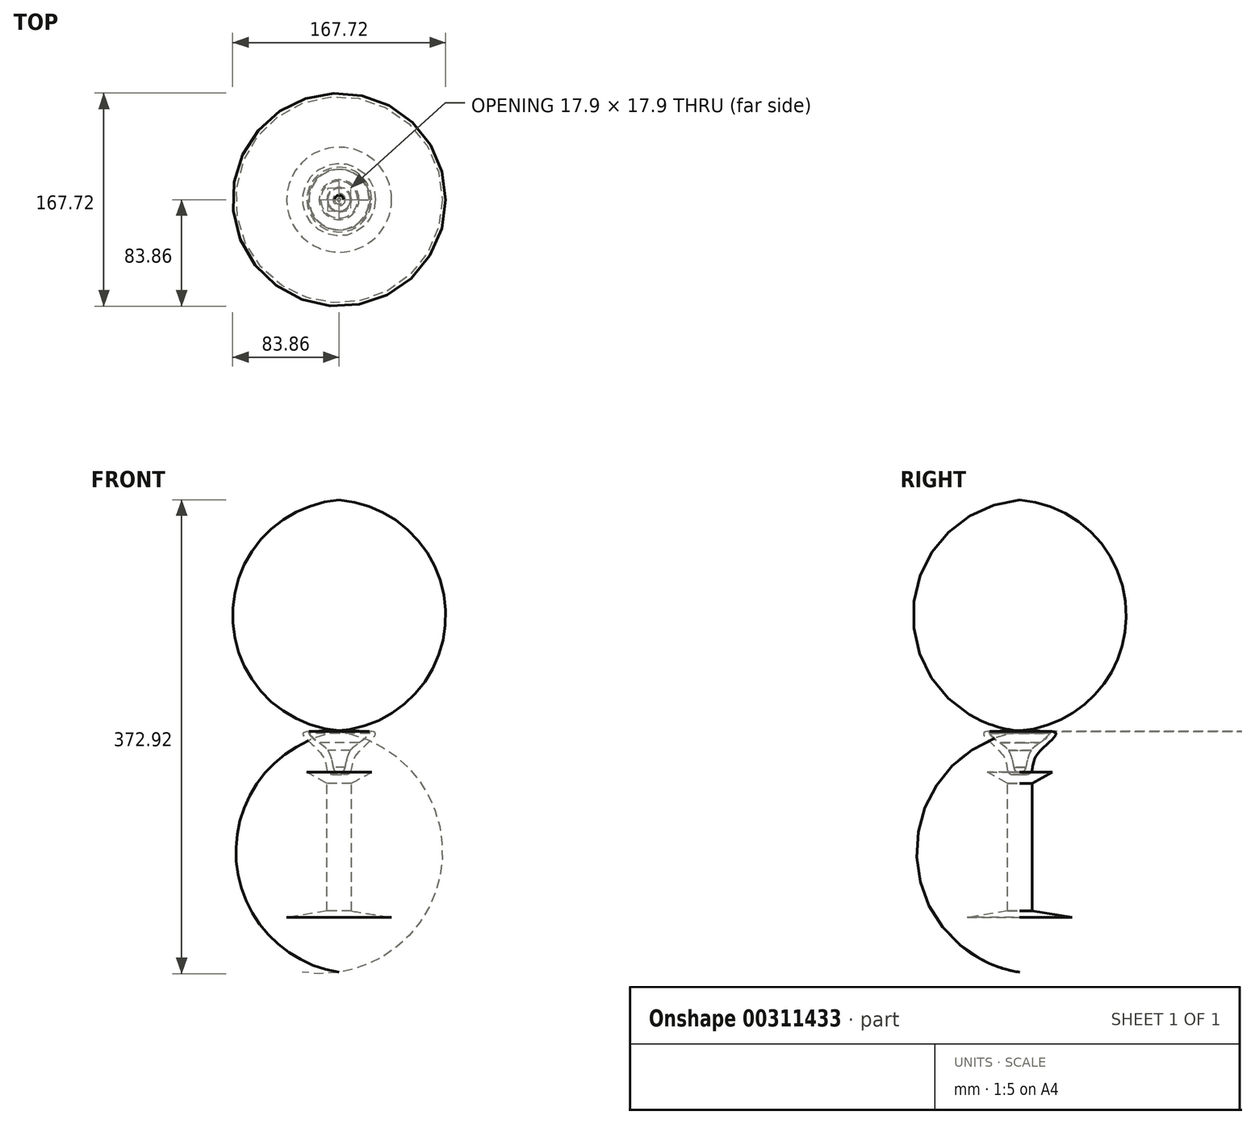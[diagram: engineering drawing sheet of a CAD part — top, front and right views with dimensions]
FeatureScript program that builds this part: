
annotation { "Feature Type Name" : "Feature", "Feature Type Description" : "" }
export const myFeature = defineFeature(function(context is Context, id is Id, definition is map)
    precondition{}
    {
        {
            var Q0;
            Q0=qCreatedBy(makeId("Front.planeOp"),FACE);
            var sketch = newSketch(context, id + "F0", { "sketchPlane" : qUnion([Q0])});
            skLineSegment(sketch, "E0", {"start": v(0, 76.77) * mm, "end": v(0, -76.43) * mm, "construction": true});
            skLineSegment(sketch, "E1", {"start": v(0, -76.43) * mm, "end": v(-41.31, -76.43) * mm});
            skLineSegment(sketch, "E2", {"start": v(-9.64, -71.26) * mm, "end": v(-9.64, 29.26) * mm});
            skLineSegment(sketch, "E3", {"start": v(-25.48, 37.87) * mm, "end": v(-8.95, 37.87) * mm});
            skLineSegment(sketch, "E4", {"start": v(0, 37.87) * mm, "end": v(0, -76.43) * mm});
            skFitSpline(sketch, "E5", {"points": [v(0, 37.87) * mm, v(-4.78, 41.96) * mm, v(-5.64, 46.27) * mm, v(-8.95, 55.08) * mm, v(-15.6, 61.06) * mm, v(-23.75, 68.51) * mm, v(0, 70.58) * mm, v(33.4, 67.82) * mm, v(0, 37.87) * mm]});
            skLineSegment(sketch, "E6", {"start": v(0, 70.58) * mm, "end": v(0, 37.87) * mm});
            skFitSpline(sketch, "E7", {"points": [v(-8.95, 37.87) * mm, v(-12.74, 50.44) * mm, v(-28.57, 68.34) * mm, v(0, 70.58) * mm, v(24.1, 70.58) * mm, v(0, 37.87) * mm, v(-8.95, 37.87) * mm]});
            skLineSegment(sketch, "E8.trimOffspring", {"start": v(-1.04, 37.87) * mm, "end": v(0, 37.87) * mm});
            skLineSegment(sketch, "E9", {"start": v(-41.31, -76.43) * mm, "end": v(-9.64, -71.26) * mm});
            skLineSegment(sketch, "E10", {"start": v(-9.64, 29.26) * mm, "end": v(-25.48, 37.87) * mm});
            skPoint(sketch, "E10.endSnap0", {"position": v(-25.48, 33.57) * mm});
            skLineSegment(sketch, "E11", {"start": v(-25.48, 37.87) * mm, "end": v(-1.04, 37.87) * mm});
            skPoint(sketch, "E12.orphan", {"position": v(-41.31, 37.87) * mm});
            skFitSpline(sketch, "E13", {"points": [v(-1.04, 37.87) * mm, v(-4.78, 41.96) * mm, v(-5.64, 46.27) * mm, v(-8.95, 55.08) * mm, v(-15.6, 61.06) * mm, v(-23.75, 68.51) * mm, v(-23.75, 70.2) * mm, v(19.65, 61.06) * mm, v(-1.04, 37.87) * mm]});
            skSolve(sketch);
        }
        {
            var Q0;
            Q0=makeQuery(id+"F0.imprint","IMPRINT",FACE,{"disambiguationData":[TD([[makeQuery(id+"F0.imprint","IMPRINT",EDGE,{"derivedFrom":sQuery(id+"F0.wireOp",EDGE,"E1")}),-1.0]])]});
            var Q1;
            Q1=sQuery(id+"F0.wireOp",EDGE,"E4");
            revolve(context, id + "F1", {"entities" : qUnion([Q0]), "axis" : qUnion([Q1]), "revolveType" : RevolveType.FULL});
        }
        {
            var Q0;
            Q0=makeQuery(id+"F0.imprint","IMPRINT",FACE,{"disambiguationData":[TD([[makeQuery(id+"F0.imprint","IMPRINT",EDGE,{"derivedFrom":sQuery(id+"F0.wireOp",EDGE,"E5")}),-1.0]])]});
            var Q1;
            Q1=sQuery(id+"F0.wireOp",EDGE,"E6");
            revolve(context, id + "F2", {"entities" : qUnion([Q0]), "axis" : qUnion([Q1]), "revolveType" : RevolveType.FULL});
        }
        {
            var Q0;
            Q0=makeQuery(id+"F0.imprint","IMPRINT",FACE,{"disambiguationData":[TD([[makeQuery(id+"F0.imprint","IMPRINT",EDGE,{"derivedFrom":sQuery(id+"F0.wireOp",EDGE,"E2")}),-1.0]])]});
            var Q1;
            Q1=sQuery(id+"F0.wireOp",EDGE,"E4");
            revolve(context, id + "F3", {"entities" : qUnion([Q0]), "axis" : qUnion([Q1]), "revolveType" : RevolveType.FULL});
        }
        {
            var Q0;
            {var subQ1=sQuery(id+"F0.wireOp",EDGE,"E6");Q0=makeQuery(id+"F0.imprint","IMPRINT",FACE,{"disambiguationData":[TD([[makeQuery(id+"F0.imprint","IMPRINT",EDGE,{"derivedFrom":subQ1}),-1.0]])]});}
            var Q1;
            {var subQ0=sQuery(id+"F0.wireOp",EDGE,"E11");var subQ1=sQuery(id+"F0.wireOp",EDGE,"E7");var subQ2=makeQuery(id+"F0.imprint","INTERSECT",VERTEX,{"derivedFrom":[subQ1,subQ0]});Q1=makeQuery(id+"F0.imprint","IMPRINT",FACE,{"disambiguationData":[TD([[makeQuery(id+"F0.imprint","IMPRINT",EDGE,{"disambiguationData":[TD([[subQ2,-1.0]])],"derivedFrom":subQ1}),-1.0]])]});}
            var Q2;
            Q2=sQuery(id+"F0.wireOp",EDGE,"E7");
            var Q3;
            Q3=sQuery(id+"F0.wireOp",EDGE,"E6");
            revolve(context, id + "F4", {"entities" : qUnion([Q0, Q1]), "surfaceEntities" : qUnion([Q2]), "axis" : qUnion([Q3]), "revolveType" : RevolveType.FULL});
        }
    });
